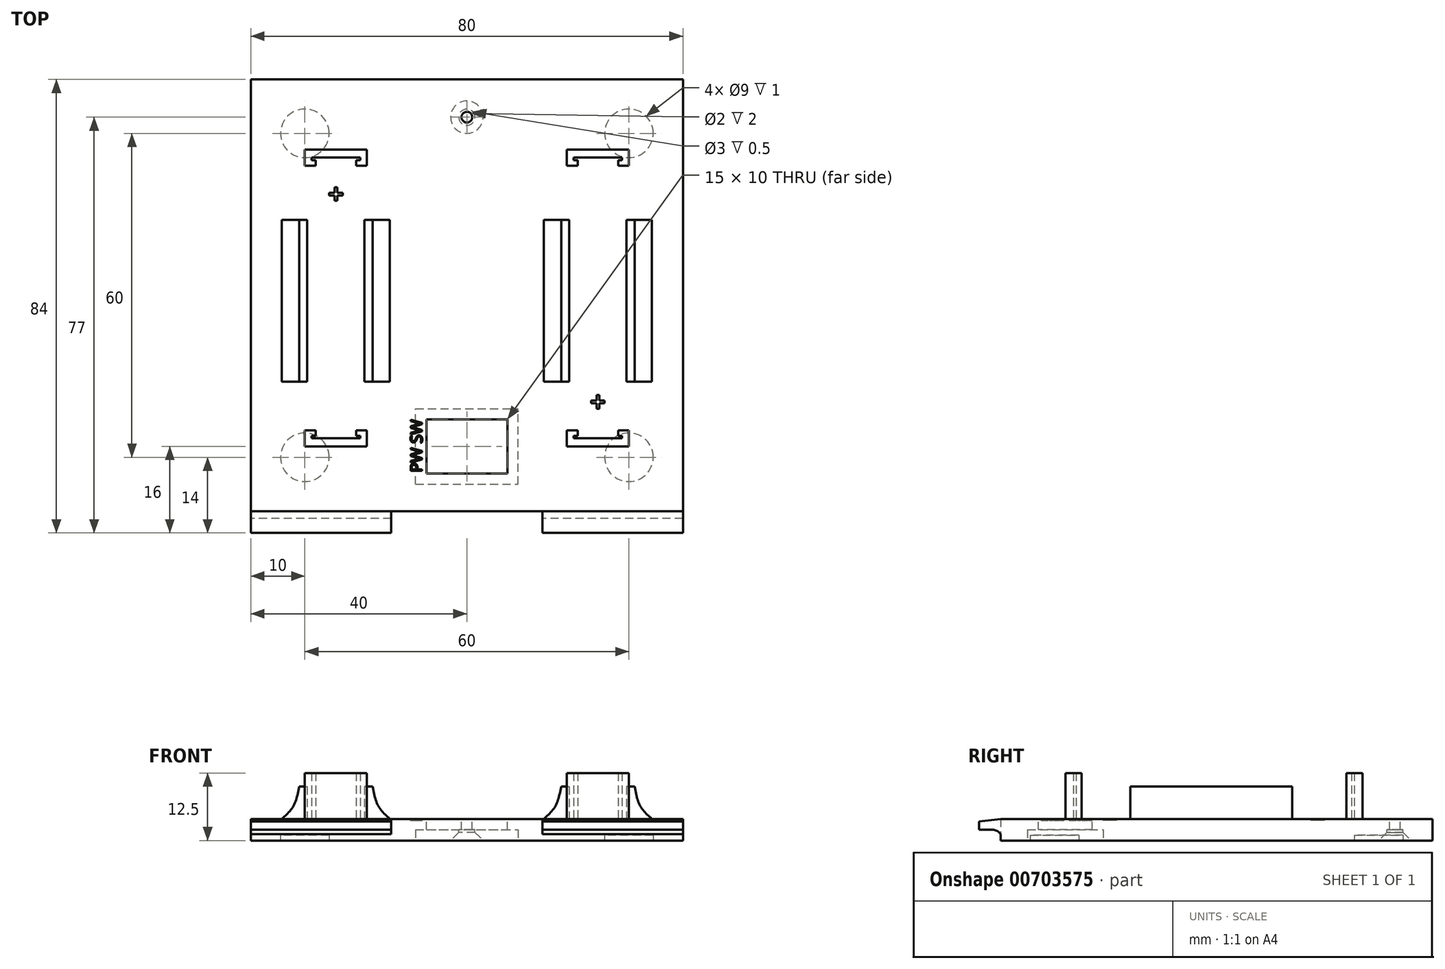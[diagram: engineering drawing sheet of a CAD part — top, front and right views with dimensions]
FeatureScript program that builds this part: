
annotation { "Feature Type Name" : "Feature", "Feature Type Description" : "" }
export const myFeature = defineFeature(function(context is Context, id is Id, definition is map)
    precondition{}
    {
        {
            var Q0;
            Q0=qCreatedBy(makeId("Top.planeOp"),FACE);
            var sketch = newSketch(context, id + "F0", { "sketchPlane" : qUnion([Q0])});
            skLineSegment(sketch, "E0.bottom", {"start": v(-40, 40) * mm, "end": v(40, 40) * mm});
            skLineSegment(sketch, "E0.top", {"start": v(-40, -40) * mm, "end": v(40, -40) * mm});
            skLineSegment(sketch, "E0.left", {"start": v(-40, 40) * mm, "end": v(-40, -40) * mm});
            skLineSegment(sketch, "E0.right", {"start": v(40, 40) * mm, "end": v(40, -40) * mm});
            skLineSegment(sketch, "E1.bottom", {"start": v(-40, -40) * mm, "end": v(-20, -40) * mm});
            skLineSegment(sketch, "E1.top", {"start": v(-40, -44) * mm, "end": v(-20, -44) * mm});
            skLineSegment(sketch, "E1.left", {"start": v(-40, -40) * mm, "end": v(-40, -44) * mm});
            skLineSegment(sketch, "E1.right", {"start": v(-20, -40) * mm, "end": v(-20, -44) * mm});
            skLineSegment(sketch, "E2.bottom", {"start": v(20, -40) * mm, "end": v(40, -40) * mm});
            skLineSegment(sketch, "E2.top", {"start": v(20, -44) * mm, "end": v(40, -44) * mm});
            skLineSegment(sketch, "E2.left", {"start": v(20, -40) * mm, "end": v(20, -44) * mm});
            skLineSegment(sketch, "E2.right", {"start": v(40, -40) * mm, "end": v(40, -44) * mm});
            skLineSegment(sketch, "E3", {"start": v(-20, -44) * mm, "end": v(20, -44) * mm});
            skLineSegment(sketch, "E4", {"start": v(-20, -40) * mm, "end": v(20, -40) * mm});
            skLineSegment(sketch, "E5", {"start": v(-14, -44) * mm, "end": v(-14, -40) * mm});
            skLineSegment(sketch, "E6", {"start": v(14, -44) * mm, "end": v(14, -40) * mm});
            skPoint(sketch, "E6.endSnap0", {"position": v(0, -40) * mm});
            skSolve(sketch);
        }
        {
            var Q0;
            Q0=makeQuery(id+"F0.imprint","IMPRINT",FACE,{"disambiguationData":[TD([[makeQuery(id+"F0.imprint","IMPRINT",EDGE,{"derivedFrom":sQuery(id+"F0.wireOp",EDGE,"E0.bottom")}),-1.0]])]});
            extrude(context, id + "F1", {"entities" : qUnion([Q0]), "depth" : 4 * mm, "offsetDistance" : 25 * mm});
        }
        {
            var Q0;
            Q0=makeQuery(id+"F1.opExtrude","CAP_FACE",FACE,{"disambiguationData":[OSD([sQuery(id+"F0.wireOp",EDGE,"E0.bottom"),sQuery(id+"F0.wireOp",EDGE,"E0.top"),sQuery(id+"F0.wireOp",EDGE,"E0.left"),sQuery(id+"F0.wireOp",EDGE,"E0.right")])],"isStart":false});
            var sketch = newSketch(context, id + "F2", { "sketchPlane" : qUnion([Q0])});
            skLineSegment(sketch, "E7.bottom", {"start": v(-30, 27) * mm, "end": v(-28, 27) * mm});
            skLineSegment(sketch, "E7.top", {"start": v(-30, 24) * mm, "end": v(-28, 24) * mm});
            skLineSegment(sketch, "E7.left", {"start": v(-30, 27) * mm, "end": v(-30, 24) * mm});
            skLineSegment(sketch, "E7.right", {"start": v(-28, 27) * mm, "end": v(-28, 24) * mm});
            skLineSegment(sketch, "E8.bottom", {"start": v(-20.5, 27) * mm, "end": v(-18.5, 27) * mm});
            skLineSegment(sketch, "E8.top", {"start": v(-20.5, 24) * mm, "end": v(-18.5, 24) * mm});
            skLineSegment(sketch, "E8.left", {"start": v(-20.5, 27) * mm, "end": v(-20.5, 24) * mm});
            skLineSegment(sketch, "E8.right", {"start": v(-18.5, 27) * mm, "end": v(-18.5, 24) * mm});
            skLineSegment(sketch, "E9", {"start": v(-28, 27) * mm, "end": v(-20.5, 27) * mm});
            skLineSegment(sketch, "E10", {"start": v(-28, 25) * mm, "end": v(-20.5, 25) * mm, "construction": true});
            skLineSegment(sketch, "E11", {"start": v(-28, 25.5) * mm, "end": v(-20.5, 25.5) * mm});
            skLineSegment(sketch, "E12", {"start": v(-28, 25.5) * mm, "end": v(-28.75, 25.5) * mm});
            skLineSegment(sketch, "E13", {"start": v(-28.75, 25.5) * mm, "end": v(-28.75, 25) * mm});
            skLineSegment(sketch, "E14", {"start": v(-28.75, 25) * mm, "end": v(-28, 25) * mm});
            skLineSegment(sketch, "E15", {"start": v(-20.5, 25.5) * mm, "end": v(-19.75, 25.5) * mm});
            skLineSegment(sketch, "E16", {"start": v(-19.75, 25.5) * mm, "end": v(-19.75, 25) * mm});
            skLineSegment(sketch, "E17", {"start": v(-19.75, 25) * mm, "end": v(-20.5, 25) * mm});
            skLineSegment(sketch, "E18.bottom", {"start": v(-18.5, -28) * mm, "end": v(-20.5, -28) * mm});
            skLineSegment(sketch, "E18.top", {"start": v(-18.5, -25) * mm, "end": v(-20.5, -25) * mm});
            skLineSegment(sketch, "E18.left", {"start": v(-18.5, -28) * mm, "end": v(-18.5, -25) * mm});
            skLineSegment(sketch, "E18.right", {"start": v(-20.5, -28) * mm, "end": v(-20.5, -25) * mm});
            skLineSegment(sketch, "E19.bottom", {"start": v(-28, -28) * mm, "end": v(-30, -28) * mm});
            skLineSegment(sketch, "E19.top", {"start": v(-28, -25) * mm, "end": v(-30, -25) * mm});
            skLineSegment(sketch, "E19.left", {"start": v(-28, -28) * mm, "end": v(-28, -25) * mm});
            skLineSegment(sketch, "E19.right", {"start": v(-30, -28) * mm, "end": v(-30, -25) * mm});
            skLineSegment(sketch, "E20", {"start": v(-20.5, -28) * mm, "end": v(-28, -28) * mm});
            skLineSegment(sketch, "E21", {"start": v(-20.5, -26) * mm, "end": v(-28, -26) * mm, "construction": true});
            skLineSegment(sketch, "E22", {"start": v(-20.5, -26.5) * mm, "end": v(-28, -26.5) * mm});
            skLineSegment(sketch, "E23", {"start": v(-20.5, -26.5) * mm, "end": v(-19.75, -26.5) * mm});
            skLineSegment(sketch, "E24", {"start": v(-19.75, -26.5) * mm, "end": v(-19.75, -26) * mm});
            skLineSegment(sketch, "E25", {"start": v(-19.75, -26) * mm, "end": v(-20.5, -26) * mm});
            skLineSegment(sketch, "E26", {"start": v(-28, -26.5) * mm, "end": v(-28.75, -26.5) * mm});
            skLineSegment(sketch, "E27", {"start": v(-28.75, -26.5) * mm, "end": v(-28.75, -26) * mm});
            skLineSegment(sketch, "E28", {"start": v(-28.75, -26) * mm, "end": v(-28, -26) * mm});
            skLineSegment(sketch, "E29.bottom", {"start": v(18.5, 27) * mm, "end": v(20.5, 27) * mm});
            skLineSegment(sketch, "E29.top", {"start": v(18.5, 24) * mm, "end": v(20.5, 24) * mm});
            skLineSegment(sketch, "E29.left", {"start": v(18.5, 27) * mm, "end": v(18.5, 24) * mm});
            skLineSegment(sketch, "E29.right", {"start": v(20.5, 27) * mm, "end": v(20.5, 24) * mm});
            skLineSegment(sketch, "E30.bottom", {"start": v(28, 27) * mm, "end": v(30, 27) * mm});
            skLineSegment(sketch, "E30.top", {"start": v(28, 24) * mm, "end": v(30, 24) * mm});
            skLineSegment(sketch, "E30.left", {"start": v(28, 27) * mm, "end": v(28, 24) * mm});
            skLineSegment(sketch, "E30.right", {"start": v(30, 27) * mm, "end": v(30, 24) * mm});
            skLineSegment(sketch, "E31", {"start": v(20.5, 27) * mm, "end": v(28, 27) * mm});
            skLineSegment(sketch, "E32", {"start": v(20.5, 25) * mm, "end": v(28, 25) * mm, "construction": true});
            skLineSegment(sketch, "E33", {"start": v(20.5, 25.5) * mm, "end": v(28, 25.5) * mm});
            skLineSegment(sketch, "E34", {"start": v(20.5, 25.5) * mm, "end": v(19.75, 25.5) * mm});
            skLineSegment(sketch, "E35", {"start": v(19.75, 25.5) * mm, "end": v(19.75, 25) * mm});
            skLineSegment(sketch, "E36", {"start": v(19.75, 25) * mm, "end": v(20.5, 25) * mm});
            skLineSegment(sketch, "E37", {"start": v(28, 25.5) * mm, "end": v(28.75, 25.5) * mm});
            skLineSegment(sketch, "E38", {"start": v(28.75, 25.5) * mm, "end": v(28.75, 25) * mm});
            skLineSegment(sketch, "E39", {"start": v(28.75, 25) * mm, "end": v(28, 25) * mm});
            skLineSegment(sketch, "E40.bottom", {"start": v(30, -28) * mm, "end": v(28, -28) * mm});
            skLineSegment(sketch, "E40.top", {"start": v(30, -25) * mm, "end": v(28, -25) * mm});
            skLineSegment(sketch, "E40.left", {"start": v(30, -28) * mm, "end": v(30, -25) * mm});
            skLineSegment(sketch, "E40.right", {"start": v(28, -28) * mm, "end": v(28, -25) * mm});
            skLineSegment(sketch, "E41.bottom", {"start": v(20.5, -28) * mm, "end": v(18.5, -28) * mm});
            skLineSegment(sketch, "E41.top", {"start": v(20.5, -25) * mm, "end": v(18.5, -25) * mm});
            skLineSegment(sketch, "E41.left", {"start": v(20.5, -28) * mm, "end": v(20.5, -25) * mm});
            skLineSegment(sketch, "E41.right", {"start": v(18.5, -28) * mm, "end": v(18.5, -25) * mm});
            skLineSegment(sketch, "E42", {"start": v(28, -28) * mm, "end": v(20.5, -28) * mm});
            skLineSegment(sketch, "E43", {"start": v(28, -26) * mm, "end": v(20.5, -26) * mm, "construction": true});
            skLineSegment(sketch, "E44", {"start": v(28, -26.5) * mm, "end": v(20.5, -26.5) * mm});
            skLineSegment(sketch, "E45", {"start": v(28, -26.5) * mm, "end": v(28.75, -26.5) * mm});
            skLineSegment(sketch, "E46", {"start": v(28.75, -26.5) * mm, "end": v(28.75, -26) * mm});
            skLineSegment(sketch, "E47", {"start": v(28.75, -26) * mm, "end": v(28, -26) * mm});
            skLineSegment(sketch, "E48", {"start": v(20.5, -26.5) * mm, "end": v(19.75, -26.5) * mm});
            skLineSegment(sketch, "E49", {"start": v(19.75, -26.5) * mm, "end": v(19.75, -26) * mm});
            skLineSegment(sketch, "E50", {"start": v(19.75, -26) * mm, "end": v(20.5, -26) * mm});
            skLineSegment(sketch, "E51", {"start": v(-18.5, 27) * mm, "end": v(18.5, 27) * mm, "construction": true});
            skLineSegment(sketch, "E52", {"start": v(-24.25, 25) * mm, "end": v(-24.25, -26) * mm, "construction": true});
            skLineSegment(sketch, "E53", {"start": v(24.25, 25) * mm, "end": v(24.25, -26) * mm, "construction": true});
            skLineSegment(sketch, "E54.bottom", {"start": v(-31.05, 14) * mm, "end": v(-29.55, 14) * mm});
            skLineSegment(sketch, "E54.top", {"start": v(-31.05, 4) * mm, "end": v(-29.55, 4) * mm});
            skLineSegment(sketch, "E54.left", {"start": v(-31.05, 14) * mm, "end": v(-31.05, 4) * mm});
            skLineSegment(sketch, "E54.right", {"start": v(-29.55, 14) * mm, "end": v(-29.55, 4) * mm});
            skLineSegment(sketch, "E55", {"start": v(-30, 24) * mm, "end": v(-42.81, 24) * mm, "construction": true});
            skLineSegment(sketch, "E56.bottom", {"start": v(-31.05, -6) * mm, "end": v(-29.55, -6) * mm});
            skLineSegment(sketch, "E56.top", {"start": v(-31.05, -16) * mm, "end": v(-29.55, -16) * mm});
            skLineSegment(sketch, "E56.left", {"start": v(-31.05, -6) * mm, "end": v(-31.05, -16) * mm});
            skLineSegment(sketch, "E56.right", {"start": v(-29.55, -6) * mm, "end": v(-29.55, -16) * mm});
            skLineSegment(sketch, "E57.MirrorCS", {"start": v(-18.95, 14) * mm, "end": v(-18.95, 4) * mm});
            skLineSegment(sketch, "E58.MirrorCS", {"start": v(-17.45, 14) * mm, "end": v(-17.45, 4) * mm});
            skLineSegment(sketch, "E59.MirrorCS", {"start": v(-17.45, 14) * mm, "end": v(-18.95, 14) * mm});
            skLineSegment(sketch, "E60.MirrorCS", {"start": v(-17.45, 4) * mm, "end": v(-18.95, 4) * mm});
            skLineSegment(sketch, "E61.MirrorCS", {"start": v(-18.95, -6) * mm, "end": v(-18.95, -16) * mm});
            skLineSegment(sketch, "E62.MirrorCS", {"start": v(-17.45, -6) * mm, "end": v(-17.45, -16) * mm});
            skLineSegment(sketch, "E63.MirrorCS", {"start": v(-17.45, -6) * mm, "end": v(-18.95, -6) * mm});
            skLineSegment(sketch, "E64.MirrorCS", {"start": v(-17.45, -16) * mm, "end": v(-18.95, -16) * mm});
            skLineSegment(sketch, "E65", {"start": v(18.5, 24) * mm, "end": v(3.37, 24) * mm, "construction": true});
            skLineSegment(sketch, "E66.bottom", {"start": v(17.45, 14) * mm, "end": v(18.95, 14) * mm});
            skLineSegment(sketch, "E66.top", {"start": v(17.45, 4) * mm, "end": v(18.95, 4) * mm});
            skLineSegment(sketch, "E66.left", {"start": v(17.45, 14) * mm, "end": v(17.45, 4) * mm});
            skLineSegment(sketch, "E66.right", {"start": v(18.95, 14) * mm, "end": v(18.95, 4) * mm});
            skLineSegment(sketch, "E67.bottom", {"start": v(17.45, -6) * mm, "end": v(18.95, -6) * mm});
            skLineSegment(sketch, "E67.top", {"start": v(17.45, -16) * mm, "end": v(18.95, -16) * mm});
            skLineSegment(sketch, "E67.left", {"start": v(17.45, -6) * mm, "end": v(17.45, -16) * mm});
            skLineSegment(sketch, "E67.right", {"start": v(18.95, -6) * mm, "end": v(18.95, -16) * mm});
            skLineSegment(sketch, "E68.MirrorCS", {"start": v(29.55, 14) * mm, "end": v(29.55, 4) * mm});
            skLineSegment(sketch, "E69.MirrorCS", {"start": v(31.05, 14) * mm, "end": v(31.05, 4) * mm});
            skLineSegment(sketch, "E70.MirrorCS", {"start": v(31.05, 4) * mm, "end": v(29.55, 4) * mm});
            skLineSegment(sketch, "E71.MirrorCS", {"start": v(31.05, 14) * mm, "end": v(29.55, 14) * mm});
            skLineSegment(sketch, "E72.MirrorCS", {"start": v(31.05, -6) * mm, "end": v(29.55, -6) * mm});
            skLineSegment(sketch, "E73.MirrorCS", {"start": v(29.55, -6) * mm, "end": v(29.55, -16) * mm});
            skLineSegment(sketch, "E74.MirrorCS", {"start": v(31.05, -6) * mm, "end": v(31.05, -16) * mm});
            skLineSegment(sketch, "E75.MirrorCS", {"start": v(31.05, -16) * mm, "end": v(29.55, -16) * mm});
            skLineSegment(sketch, "E76", {"start": v(-28, -25) * mm, "end": v(-20.5, -25) * mm, "construction": true});
            skLineSegment(sketch, "E77", {"start": v(20.5, -25) * mm, "end": v(28, -25) * mm, "construction": true});
            skLineSegment(sketch, "E78", {"start": v(20.5, 24) * mm, "end": v(28, 24) * mm, "construction": true});
            skLineSegment(sketch, "E79", {"start": v(-28, 24) * mm, "end": v(-20.5, 24) * mm, "construction": true});
            skLineSegment(sketch, "E80.bottom", {"start": v(-24.5, 20) * mm, "end": v(-24, 20) * mm});
            skLineSegment(sketch, "E80.top", {"start": v(-24.5, 17.5) * mm, "end": v(-24, 17.5) * mm});
            skLineSegment(sketch, "E80.left", {"start": v(-24.5, 20) * mm, "end": v(-24.5, 19) * mm});
            skLineSegment(sketch, "E80.right", {"start": v(-24, 20) * mm, "end": v(-24, 19) * mm});
            skLineSegment(sketch, "E81.bottom", {"start": v(-23, 19) * mm, "end": v(-24, 19) * mm});
            skLineSegment(sketch, "E81.top", {"start": v(-23, 18.5) * mm, "end": v(-24, 18.5) * mm});
            skLineSegment(sketch, "E81.left", {"start": v(-23, 19) * mm, "end": v(-23, 18.5) * mm});
            skLineSegment(sketch, "E81.right", {"start": v(-25.5, 19) * mm, "end": v(-25.5, 18.5) * mm});
            skLineSegment(sketch, "E82", {"start": v(-25.5, 18.75) * mm, "end": v(-23, 18.75) * mm, "construction": true});
            skLineSegment(sketch, "E83", {"start": v(-24.25, 20) * mm, "end": v(-24.25, 17.5) * mm, "construction": true});
            skLineSegment(sketch, "E84.trimOffspring", {"start": v(-24.5, 18.5) * mm, "end": v(-24.5, 17.5) * mm});
            skLineSegment(sketch, "E85.trimOffspring", {"start": v(-24.5, 18.5) * mm, "end": v(-25.5, 18.5) * mm});
            skLineSegment(sketch, "E86.trimOffspring", {"start": v(-24, 18.5) * mm, "end": v(-24, 17.5) * mm});
            skLineSegment(sketch, "E87.trimOffspring", {"start": v(-24.5, 19) * mm, "end": v(-25.5, 19) * mm});
            skLineSegment(sketch, "E88.bottom", {"start": v(24, -18.5) * mm, "end": v(24.5, -18.5) * mm});
            skLineSegment(sketch, "E88.top", {"start": v(24, -21) * mm, "end": v(24.5, -21) * mm});
            skLineSegment(sketch, "E88.left", {"start": v(24, -18.5) * mm, "end": v(24, -19.5) * mm});
            skLineSegment(sketch, "E88.right", {"start": v(24.5, -18.5) * mm, "end": v(24.5, -19.5) * mm});
            skLineSegment(sketch, "E89.bottom", {"start": v(25.5, -19.5) * mm, "end": v(24.5, -19.5) * mm});
            skLineSegment(sketch, "E89.top", {"start": v(25.5, -20) * mm, "end": v(24.5, -20) * mm});
            skLineSegment(sketch, "E89.left", {"start": v(25.5, -19.5) * mm, "end": v(25.5, -20) * mm});
            skLineSegment(sketch, "E89.right", {"start": v(23, -19.5) * mm, "end": v(23, -20) * mm});
            skLineSegment(sketch, "E90", {"start": v(23, -19.75) * mm, "end": v(25.5, -19.75) * mm, "construction": true});
            skLineSegment(sketch, "E91", {"start": v(24.25, -18.5) * mm, "end": v(24.25, -21) * mm, "construction": true});
            skLineSegment(sketch, "E92.trimOffspring", {"start": v(24, -20) * mm, "end": v(24, -21) * mm});
            skLineSegment(sketch, "E93.trimOffspring", {"start": v(24, -20) * mm, "end": v(23, -20) * mm});
            skLineSegment(sketch, "E94.trimOffspring", {"start": v(24.5, -20) * mm, "end": v(24.5, -21) * mm});
            skLineSegment(sketch, "E95.trimOffspring", {"start": v(24, -19.5) * mm, "end": v(23, -19.5) * mm});
            skLineSegment(sketch, "E96", {"start": v(-31.05, 4) * mm, "end": v(-31.05, -6) * mm});
            skLineSegment(sketch, "E97", {"start": v(-29.55, 4) * mm, "end": v(-29.55, -6) * mm});
            skLineSegment(sketch, "E98", {"start": v(-18.95, 4) * mm, "end": v(-18.95, -6) * mm});
            skLineSegment(sketch, "E99", {"start": v(-17.45, 4) * mm, "end": v(-17.45, -6) * mm});
            skLineSegment(sketch, "E100", {"start": v(29.55, 4) * mm, "end": v(29.55, -6) * mm});
            skLineSegment(sketch, "E101", {"start": v(31.05, 4) * mm, "end": v(31.05, -6) * mm});
            skLineSegment(sketch, "E102", {"start": v(17.45, 4) * mm, "end": v(17.45, -6) * mm});
            skLineSegment(sketch, "E103", {"start": v(18.95, 4) * mm, "end": v(18.95, -6) * mm});
            skSolve(sketch);
        }
        {
            var Q0;
            Q0=makeQuery(id+"F2.imprint","IMPRINT",FACE,{"disambiguationData":[TD([[makeQuery(id+"F2.imprint","IMPRINT",EDGE,{"derivedFrom":sQuery(id+"F2.wireOp",EDGE,"E56.bottom")}),-1.0]])]});
            var Q1;
            Q1=makeQuery(id+"F2.imprint","IMPRINT",FACE,{"disambiguationData":[TD([[makeQuery(id+"F2.imprint","IMPRINT",EDGE,{"derivedFrom":sQuery(id+"F2.wireOp",EDGE,"E61.MirrorCS")}),1.0]])]});
            var Q2;
            Q2=makeQuery(id+"F2.imprint","IMPRINT",FACE,{"disambiguationData":[TD([[makeQuery(id+"F2.imprint","IMPRINT",EDGE,{"derivedFrom":sQuery(id+"F2.wireOp",EDGE,"E57.MirrorCS")}),1.0]])]});
            var Q3;
            Q3=makeQuery(id+"F2.imprint","IMPRINT",FACE,{"disambiguationData":[TD([[makeQuery(id+"F2.imprint","IMPRINT",EDGE,{"derivedFrom":sQuery(id+"F2.wireOp",EDGE,"E54.bottom")}),-1.0]])]});
            var Q4;
            Q4=makeQuery(id+"F2.imprint","IMPRINT",FACE,{"disambiguationData":[TD([[makeQuery(id+"F2.imprint","IMPRINT",EDGE,{"derivedFrom":sQuery(id+"F2.wireOp",EDGE,"E67.bottom")}),-1.0]])]});
            var Q5;
            Q5=makeQuery(id+"F2.imprint","IMPRINT",FACE,{"disambiguationData":[TD([[makeQuery(id+"F2.imprint","IMPRINT",EDGE,{"derivedFrom":sQuery(id+"F2.wireOp",EDGE,"E66.bottom")}),-1.0]])]});
            var Q6;
            Q6=makeQuery(id+"F2.imprint","IMPRINT",FACE,{"disambiguationData":[TD([[makeQuery(id+"F2.imprint","IMPRINT",EDGE,{"derivedFrom":sQuery(id+"F2.wireOp",EDGE,"E68.MirrorCS")}),1.0]])]});
            var Q7;
            Q7=makeQuery(id+"F2.imprint","IMPRINT",FACE,{"disambiguationData":[TD([[makeQuery(id+"F2.imprint","IMPRINT",EDGE,{"derivedFrom":sQuery(id+"F2.wireOp",EDGE,"E72.MirrorCS")}),1.0]])]});
            var Q8;
            Q8=makeQuery(id+"F2.imprint","IMPRINT",FACE,{"disambiguationData":[TD([[makeQuery(id+"F2.imprint","IMPRINT",EDGE,{"derivedFrom":sQuery(id+"F2.wireOp",EDGE,"E54.top")}),-1.0]])]});
            var Q9;
            Q9=makeQuery(id+"F2.imprint","IMPRINT",FACE,{"disambiguationData":[TD([[makeQuery(id+"F2.imprint","IMPRINT",EDGE,{"derivedFrom":sQuery(id+"F2.wireOp",EDGE,"E60.MirrorCS")}),1.0]])]});
            var Q10;
            Q10=makeQuery(id+"F2.imprint","IMPRINT",FACE,{"disambiguationData":[TD([[makeQuery(id+"F2.imprint","IMPRINT",EDGE,{"derivedFrom":sQuery(id+"F2.wireOp",EDGE,"E66.top")}),-1.0]])]});
            var Q11;
            Q11=makeQuery(id+"F2.imprint","IMPRINT",FACE,{"disambiguationData":[TD([[makeQuery(id+"F2.imprint","IMPRINT",EDGE,{"derivedFrom":sQuery(id+"F2.wireOp",EDGE,"E70.MirrorCS")}),1.0]])]});
            extrude(context, id + "F3", {"entities" : qUnion([Q0, Q1, Q2, Q3, Q4, Q5, Q6, Q7, Q8, Q9, Q10, Q11]), "operationType" : NewBodyOperationType.ADD, "depth" : 6 * mm, "offsetDistance" : 25 * mm});
        }
        {
            var Q0;
            {var subQ1=sQuery(id+"F2.wireOp",EDGE,"E7.bottom");Q0=makeQuery(id+"F2.imprint","IMPRINT",FACE,{"disambiguationData":[TD([[makeQuery(id+"F2.imprint","IMPRINT",EDGE,{"derivedFrom":subQ1}),-1.0]])]});}
            var Q1;
            {var subQ0=sQuery(id+"F2.wireOp",EDGE,"E9");Q1=makeQuery(id+"F2.imprint","IMPRINT",FACE,{"disambiguationData":[TD([[makeQuery(id+"F2.imprint","IMPRINT",EDGE,{"derivedFrom":subQ0}),-1.0]])]});}
            var Q2;
            {var subQ3=sQuery(id+"F2.wireOp",EDGE,"E8.bottom");Q2=makeQuery(id+"F2.imprint","IMPRINT",FACE,{"disambiguationData":[TD([[makeQuery(id+"F2.imprint","IMPRINT",EDGE,{"derivedFrom":subQ3}),-1.0]])]});}
            var Q3;
            {var subQ1=sQuery(id+"F2.wireOp",EDGE,"E18.bottom");Q3=makeQuery(id+"F2.imprint","IMPRINT",FACE,{"disambiguationData":[TD([[makeQuery(id+"F2.imprint","IMPRINT",EDGE,{"derivedFrom":subQ1}),-1.0]])]});}
            var Q4;
            {var subQ0=sQuery(id+"F2.wireOp",EDGE,"E20");Q4=makeQuery(id+"F2.imprint","IMPRINT",FACE,{"disambiguationData":[TD([[makeQuery(id+"F2.imprint","IMPRINT",EDGE,{"derivedFrom":subQ0}),-1.0]])]});}
            var Q5;
            {var subQ3=sQuery(id+"F2.wireOp",EDGE,"E19.bottom");Q5=makeQuery(id+"F2.imprint","IMPRINT",FACE,{"disambiguationData":[TD([[makeQuery(id+"F2.imprint","IMPRINT",EDGE,{"derivedFrom":subQ3}),-1.0]])]});}
            var Q6;
            {var subQ1=sQuery(id+"F2.wireOp",EDGE,"E29.bottom");Q6=makeQuery(id+"F2.imprint","IMPRINT",FACE,{"disambiguationData":[TD([[makeQuery(id+"F2.imprint","IMPRINT",EDGE,{"derivedFrom":subQ1}),-1.0]])]});}
            var Q7;
            {var subQ0=sQuery(id+"F2.wireOp",EDGE,"E31");Q7=makeQuery(id+"F2.imprint","IMPRINT",FACE,{"disambiguationData":[TD([[makeQuery(id+"F2.imprint","IMPRINT",EDGE,{"derivedFrom":subQ0}),-1.0]])]});}
            var Q8;
            {var subQ3=sQuery(id+"F2.wireOp",EDGE,"E30.bottom");Q8=makeQuery(id+"F2.imprint","IMPRINT",FACE,{"disambiguationData":[TD([[makeQuery(id+"F2.imprint","IMPRINT",EDGE,{"derivedFrom":subQ3}),-1.0]])]});}
            var Q9;
            {var subQ1=sQuery(id+"F2.wireOp",EDGE,"E40.bottom");Q9=makeQuery(id+"F2.imprint","IMPRINT",FACE,{"disambiguationData":[TD([[makeQuery(id+"F2.imprint","IMPRINT",EDGE,{"derivedFrom":subQ1}),-1.0]])]});}
            var Q10;
            {var subQ0=sQuery(id+"F2.wireOp",EDGE,"E42");Q10=makeQuery(id+"F2.imprint","IMPRINT",FACE,{"disambiguationData":[TD([[makeQuery(id+"F2.imprint","IMPRINT",EDGE,{"derivedFrom":subQ0}),-1.0]])]});}
            var Q11;
            {var subQ3=sQuery(id+"F2.wireOp",EDGE,"E41.bottom");Q11=makeQuery(id+"F2.imprint","IMPRINT",FACE,{"disambiguationData":[TD([[makeQuery(id+"F2.imprint","IMPRINT",EDGE,{"derivedFrom":subQ3}),-1.0]])]});}
            extrude(context, id + "F4", {"entities" : qUnion([Q0, Q1, Q2, Q3, Q4, Q5, Q6, Q7, Q8, Q9, Q10, Q11]), "operationType" : NewBodyOperationType.ADD, "depth" : 8.5 * mm, "offsetDistance" : 25 * mm});
        }
        {
            var Q0;
            Q0=qCreatedBy(makeId("Front.planeOp"),FACE);
            var sketch = newSketch(context, id + "F5", { "sketchPlane" : qUnion([Q0])});
            skLineSegment(sketch, "E104.top", {"start": v(-34.24, 4) * mm, "end": v(-31.05, 4) * mm});
            skLineSegment(sketch, "E104.right", {"start": v(-31.05, 10) * mm, "end": v(-31.05, 4) * mm});
            skPoint(sketch, "E105", {"position": v(-34.24, 4) * mm});
            skFitSpline(sketch, "E106", {"points": [v(-31.05, 10) * mm, v(-32.1, 6.43) * mm, v(-34.24, 4) * mm], "startDerivative": vector(-1.38, -7.39) * mm, "endDerivative": vector(-5.04, -4.58) * mm});
            skLineSegment(sketch, "E107", {"start": v(-24.25, 13.7) * mm, "end": v(-24.25, 3.33) * mm, "construction": true});
            skFitSpline(sketch, "E108.MirrorCS", {"points": [v(-17.45, 10) * mm, v(-16.4, 6.43) * mm, v(-14.26, 4) * mm], "startDerivative": vector(1.38, -7.39) * mm, "endDerivative": vector(5.04, -4.58) * mm});
            skLineSegment(sketch, "E109", {"start": v(24.25, 13.97) * mm, "end": v(24.25, 2.5) * mm, "construction": true});
            skLineSegment(sketch, "E110.MirrorCS", {"start": v(-17.45, 10) * mm, "end": v(-17.45, 4) * mm});
            skLineSegment(sketch, "E111.MirrorCS", {"start": v(-14.26, 4) * mm, "end": v(-17.45, 4) * mm});
            skFitSpline(sketch, "E112.MirrorCS", {"points": [v(17.45, 10) * mm, v(16.4, 6.43) * mm, v(14.26, 4) * mm], "startDerivative": vector(-1.38, -7.39) * mm, "endDerivative": vector(-5.04, -4.58) * mm});
            skFitSpline(sketch, "E113.MirrorCS", {"points": [v(31.05, 10) * mm, v(32.1, 6.43) * mm, v(34.24, 4) * mm], "startDerivative": vector(1.38, -7.39) * mm, "endDerivative": vector(5.04, -4.58) * mm});
            skLineSegment(sketch, "E114.MirrorCS", {"start": v(34.24, 4) * mm, "end": v(31.05, 4) * mm});
            skLineSegment(sketch, "E115.MirrorCS", {"start": v(31.05, 10) * mm, "end": v(31.05, 4) * mm});
            skLineSegment(sketch, "E116.MirrorCS", {"start": v(17.45, 10) * mm, "end": v(17.45, 4) * mm});
            skLineSegment(sketch, "E117.MirrorCS", {"start": v(14.26, 4) * mm, "end": v(17.45, 4) * mm});
            skSolve(sketch);
        }
        {
            var Q0;
            Q0=makeQuery(id+"F1.opExtrude","CAP_FACE",FACE,{"disambiguationData":[OSD([sQuery(id+"F0.wireOp",EDGE,"E0.bottom"),sQuery(id+"F0.wireOp",EDGE,"E0.top"),sQuery(id+"F0.wireOp",EDGE,"E0.left"),sQuery(id+"F0.wireOp",EDGE,"E0.right")])],"isStart":false});
            var sketch = newSketch(context, id + "F6", { "sketchPlane" : qUnion([Q0])});
            skCircle(sketch, "E118", {"center": v(0, 33) * mm, "radius": 1.5 * mm});
            skCircle(sketch, "E119", {"center": v(0, 33) * mm, "radius": 1 * mm});
            skSolve(sketch);
        }
        {
            var Q0;
            Q0=makeQuery(id+"F6.imprint","IMPRINT",FACE,{"disambiguationData":[TD([[makeQuery(id+"F6.imprint","IMPRINT",EDGE,{"derivedFrom":sQuery(id+"F6.wireOp",EDGE,"E119")}),1.0]])]});
            extrude(context, id + "F7", {"entities" : qUnion([Q0]), "operationType" : NewBodyOperationType.REMOVE, "oppositeDirection" : true, "depth" : 25 * mm, "offsetDistance" : 25 * mm});
        }
        {
            var Q0;
            Q0=makeQuery(id+"F6.imprint","IMPRINT",FACE,{"disambiguationData":[TD([[makeQuery(id+"F6.imprint","IMPRINT",EDGE,{"derivedFrom":sQuery(id+"F6.wireOp",EDGE,"E118")}),1.0]])]});
            extrude(context, id + "F8", {"entities" : qUnion([Q0]), "operationType" : NewBodyOperationType.REMOVE, "oppositeDirection" : true, "depth" : 25 * mm, "offsetDistance" : 25 * mm, "hasSecondDirection" : true, "secondDirectionOppositeDirection" : true, "secondDirectionDepth" : 2 * mm});
        }
        {
            var Q0;
            Q0=makeQuery(id+"F8.boolean.opBoolean","INTERSECT",EDGE,{"derivedFrom":[makeQuery(id+"F1.opExtrude","CAP_FACE",FACE,{"disambiguationData":[OSD([sQuery(id+"F0.wireOp",EDGE,"E0.bottom"),sQuery(id+"F0.wireOp",EDGE,"E0.top"),sQuery(id+"F0.wireOp",EDGE,"E0.left"),sQuery(id+"F0.wireOp",EDGE,"E0.right")])],"isStart":true}),makeQuery(id+"F8.opExtrude","SWEPT_FACE",FACE,{"disambiguationData":[OSD([sQuery(id+"F6.wireOp",EDGE,"E118")])]})]});
            chamfer(context, id + "F9", {"entities" : qUnion([Q0]), "width" : 1.5 * mm, "tangentPropagation" : true});
        }
        {
            var Q0;
            Q0=qCreatedBy(makeId("Right.planeOp"),FACE);
            var sketch = newSketch(context, id + "F10", { "sketchPlane" : qUnion([Q0])});
            skLineSegment(sketch, "E120", {"start": v(-44, 2) * mm, "end": v(-40, 2) * mm});
            skLineSegment(sketch, "E121", {"start": v(-44, 4) * mm, "end": v(-40, 4) * mm});
            skLineSegment(sketch, "E122", {"start": v(-44, 4) * mm, "end": v(-44, 2) * mm});
            skLineSegment(sketch, "E123", {"start": v(-40, 2) * mm, "end": v(-40, 4) * mm});
            skLineSegment(sketch, "E124", {"start": v(-47.4, 0) * mm, "end": v(-39.16, 0) * mm});
            skLineSegment(sketch, "E125", {"start": v(-40, 2) * mm, "end": v(-40, 0) * mm});
            skFitSpline(sketch, "E126", {"points": [v(-40, 1.17) * mm, v(-40.47, 1.69) * mm, v(-41.33, 2) * mm], "startDerivative": vector(-0.67, 1.12) * mm, "endDerivative": vector(-1.92, 0.56) * mm});
            skLineSegment(sketch, "E127", {"start": v(-44, 3.5) * mm, "end": v(-40, 4) * mm});
            skSolve(sketch);
        }
        {
            var Q0;
            {var subQ4=sQuery(id+"F10.wireOp",EDGE,"E123");Q0=makeQuery(id+"F10.imprint","IMPRINT",FACE,{"disambiguationData":[TD([[makeQuery(id+"F10.imprint","IMPRINT",EDGE,{"derivedFrom":subQ4}),1.0]])]});}
            var Q1;
            {var subQ3=sQuery(id+"F10.wireOp",EDGE,"E126");Q1=makeQuery(id+"F10.imprint","IMPRINT",FACE,{"disambiguationData":[TD([[makeQuery(id+"F10.imprint","IMPRINT",EDGE,{"derivedFrom":subQ3}),-1.0]])]});}
            extrude(context, id + "F11", {"entities" : qUnion([Q0, Q1]), "operationType" : NewBodyOperationType.ADD, "depth" : 40 * mm, "offsetDistance" : 25 * mm, "hasSecondDirection" : true, "secondDirectionOppositeDirection" : true, "secondDirectionDepth" : 40 * mm});
        }
        {
            var Q0;
            Q0=makeQuery(id+"F0.imprint","IMPRINT",FACE,{"disambiguationData":[TD([[makeQuery(id+"F0.imprint","IMPRINT",EDGE,{"derivedFrom":sQuery(id+"F0.wireOp",EDGE,"E1.bottom")}),-1.0]])]});
            var Q1;
            {var subQ0=sQuery(id+"F0.wireOp",EDGE,"E5");Q1=makeQuery(id+"F0.imprint","IMPRINT",FACE,{"disambiguationData":[TD([[makeQuery(id+"F0.imprint","IMPRINT",EDGE,{"derivedFrom":subQ0}),-1.0]])]});}
            var Q2;
            Q2=makeQuery(id+"F0.imprint","IMPRINT",FACE,{"disambiguationData":[TD([[makeQuery(id+"F0.imprint","IMPRINT",EDGE,{"derivedFrom":sQuery(id+"F0.wireOp",EDGE,"E2.bottom")}),-1.0]])]});
            extrude(context, id + "F12", {"entities" : qUnion([Q0, Q1, Q2]), "operationType" : NewBodyOperationType.REMOVE, "depth" : 18.6 * mm, "offsetDistance" : 25 * mm});
        }
        {
            var Q0;
            Q0=makeQuery(id+"F2.imprint","IMPRINT",FACE,{"disambiguationData":[TD([[makeQuery(id+"F2.imprint","IMPRINT",EDGE,{"derivedFrom":sQuery(id+"F2.wireOp",EDGE,"E80.bottom")}),-1.0]])]});
            var Q1;
            Q1=makeQuery(id+"F2.imprint","IMPRINT",FACE,{"disambiguationData":[TD([[makeQuery(id+"F2.imprint","IMPRINT",EDGE,{"derivedFrom":sQuery(id+"F2.wireOp",EDGE,"E88.bottom")}),-1.0]])]});
            extrude(context, id + "F13", {"entities" : qUnion([Q0, Q1]), "operationType" : NewBodyOperationType.REMOVE, "oppositeDirection" : true, "depth" : .3 * mm, "offsetDistance" : 25 * mm});
        }
        {
            var Q0;
            Q0=makeQuery(id+"F6.imprint","IMPRINT",FACE,{"disambiguationData":[TD([[makeQuery(id+"F6.imprint","IMPRINT",EDGE,{"derivedFrom":sQuery(id+"F6.wireOp",EDGE,"E118")}),-1.0]])]});
            var sketch = newSketch(context, id + "F14", { "sketchPlane" : qUnion([Q0])});
            skLineSegment(sketch, "E128.bottom", {"start": v(-7.5, -23) * mm, "end": v(7.5, -23) * mm});
            skLineSegment(sketch, "E128.top", {"start": v(-7.5, -33) * mm, "end": v(7.5, -33) * mm});
            skLineSegment(sketch, "E128.left", {"start": v(-7.5, -23) * mm, "end": v(-7.5, -33) * mm});
            skLineSegment(sketch, "E128.right", {"start": v(7.5, -23) * mm, "end": v(7.5, -33) * mm});
            skPoint(sketch, "E129", {"position": v(0, -23) * mm});
            skText(sketch, "E130", { "text": "PW SW", "fontName": "AllertaStencil-Regular.ttf"});
            const initialGuessF14  = {"E130": [-0.00882, -0.02208, 1, 0, 0.00373]};
            skSetInitialGuess(sketch, initialGuessF14);
            skSolve(sketch);
        }
        {
            var Q0;
            Q0=makeQuery(id+"F14.imprint","IMPRINT",FACE,{"disambiguationData":[TD([[makeQuery(id+"F14.imprint","IMPRINT",EDGE,{"derivedFrom":sQuery(id+"F14.wireOp",EDGE,"E128.bottom")}),-1.0]])]});
            extrude(context, id + "F15", {"entities" : qUnion([Q0]), "operationType" : NewBodyOperationType.REMOVE, "oppositeDirection" : true, "depth" : 25 * mm, "offsetDistance" : 25 * mm});
        }
        {
            var Q0;
            Q0=makeQuery(id+"F6.imprint","IMPRINT",FACE,{"disambiguationData":[TD([[makeQuery(id+"F6.imprint","IMPRINT",EDGE,{"derivedFrom":sQuery(id+"F6.wireOp",EDGE,"E118")}),-1.0]])]});
            var sketch = newSketch(context, id + "F16", { "sketchPlane" : qUnion([Q0])});
            skText(sketch, "E131", { "text": "PW SW\n", "fontName": "OpenSans-Regular.ttf"});
            const initialGuessF16  = {"E131": [-0.00828, -0.0328, 0, 1, 0.00216]};
            skSetInitialGuess(sketch, initialGuessF16);
            skSolve(sketch);
        }
        {
            var Q0;
            Q0=qSketchRegion(id+"F16",true);
            var Q1;
            Q1=qConstructionFilter(qBodyType(qCreatedBy(id+"F16",EDGE),BodyType.WIRE),ConstructionObject.NO);
            extrude(context, id + "F17", {"entities" : qUnion([Q0]), "operationType" : NewBodyOperationType.REMOVE, "surfaceOperationType" : NewSurfaceOperationType.ADD, "surfaceEntities" : qUnion([Q1]), "oppositeDirection" : true, "depth" : .3 * mm, "offsetDistance" : 25 * mm});
        }
        {
            var Q0;
            Q0=makeQuery(id+"F0.imprint","IMPRINT",FACE,{"disambiguationData":[TD([[makeQuery(id+"F0.imprint","IMPRINT",EDGE,{"derivedFrom":sQuery(id+"F0.wireOp",EDGE,"E0.bottom")}),-1.0]])]});
            var sketch = newSketch(context, id + "F18", { "sketchPlane" : qUnion([Q0])});
            skCircle(sketch, "E132", {"center": v(-30, -30) * mm, "radius": 7 * mm});
            skCircle(sketch, "E133", {"center": v(30, -30) * mm, "radius": 7 * mm});
            skCircle(sketch, "E134", {"center": v(-30, 30) * mm, "radius": 7 * mm});
            skCircle(sketch, "E135", {"center": v(30, 30) * mm, "radius": 7 * mm});
            skCircle(sketch, "E136", {"center": v(-30, -30) * mm, "radius": 4.5 * mm});
            skCircle(sketch, "E137", {"center": v(30, -30) * mm, "radius": 4.5 * mm});
            skCircle(sketch, "E138", {"center": v(-30, 30) * mm, "radius": 4.5 * mm});
            skCircle(sketch, "E139", {"center": v(30, 30) * mm, "radius": 4.5 * mm});
            skSolve(sketch);
        }
        {
            var Q0;
            Q0=makeQuery(id+"F18.imprint","IMPRINT",FACE,{"disambiguationData":[TD([[makeQuery(id+"F18.imprint","IMPRINT",EDGE,{"derivedFrom":sQuery(id+"F18.wireOp",EDGE,"E139")}),1.0]])]});
            var Q1;
            Q1=makeQuery(id+"F18.imprint","IMPRINT",FACE,{"disambiguationData":[TD([[makeQuery(id+"F18.imprint","IMPRINT",EDGE,{"derivedFrom":sQuery(id+"F18.wireOp",EDGE,"E138")}),1.0]])]});
            var Q2;
            Q2=makeQuery(id+"F18.imprint","IMPRINT",FACE,{"disambiguationData":[TD([[makeQuery(id+"F18.imprint","IMPRINT",EDGE,{"derivedFrom":sQuery(id+"F18.wireOp",EDGE,"E136")}),1.0]])]});
            var Q3;
            Q3=makeQuery(id+"F18.imprint","IMPRINT",FACE,{"disambiguationData":[TD([[makeQuery(id+"F18.imprint","IMPRINT",EDGE,{"derivedFrom":sQuery(id+"F18.wireOp",EDGE,"E137")}),1.0]])]});
            extrude(context, id + "F19", {"entities" : qUnion([Q0, Q1, Q2, Q3]), "operationType" : NewBodyOperationType.REMOVE, "oppositeDirection" : true, "depth" : -1 * mm, "offsetDistance" : 25 * mm});
        }
        {
            var Q0;
            Q0=makeQuery(id+"F1.opExtrude","CAP_FACE",FACE,{"disambiguationData":[OSD([sQuery(id+"F0.wireOp",EDGE,"E0.bottom"),sQuery(id+"F0.wireOp",EDGE,"E0.left"),sQuery(id+"F0.wireOp",EDGE,"E0.right"),sQuery(id+"F0.wireOp",EDGE,"E1.bottom"),sQuery(id+"F0.wireOp",EDGE,"E2.bottom"),sQuery(id+"F0.wireOp",EDGE,"E4")])],"isStart":true});
            var sketch = newSketch(context, id + "F20", { "sketchPlane" : qUnion([Q0])});
            skLineSegment(sketch, "E140.bottom", {"start": v(-9.5, 35) * mm, "end": v(9.5, 35) * mm});
            skLineSegment(sketch, "E140.top", {"start": v(-9.5, 21) * mm, "end": v(9.5, 21) * mm});
            skLineSegment(sketch, "E140.left", {"start": v(-9.5, 35) * mm, "end": v(-9.5, 21) * mm});
            skLineSegment(sketch, "E140.right", {"start": v(9.5, 35) * mm, "end": v(9.5, 21) * mm});
            skPoint(sketch, "E141", {"position": v(0, 35) * mm});
            skSolve(sketch);
        }
        {
            var Q0;
            Q0=qSketchRegion(id+"F20",true);
            extrude(context, id + "F21", {"entities" : qUnion([Q0]), "operationType" : NewBodyOperationType.REMOVE, "oppositeDirection" : true, "depth" : 2 * mm, "offsetDistance" : 25 * mm});
        }
        {
            var Q0;
            Q0=qSketchRegion(id+"F5",true);
            extrude(context, id + "F22", {"entities" : qUnion([Q0]), "operationType" : NewBodyOperationType.ADD, "depth" : 16 * mm, "offsetDistance" : 25 * mm, "hasSecondDirection" : true, "secondDirectionOppositeDirection" : true, "secondDirectionDepth" : 14 * mm});
        }
    });
